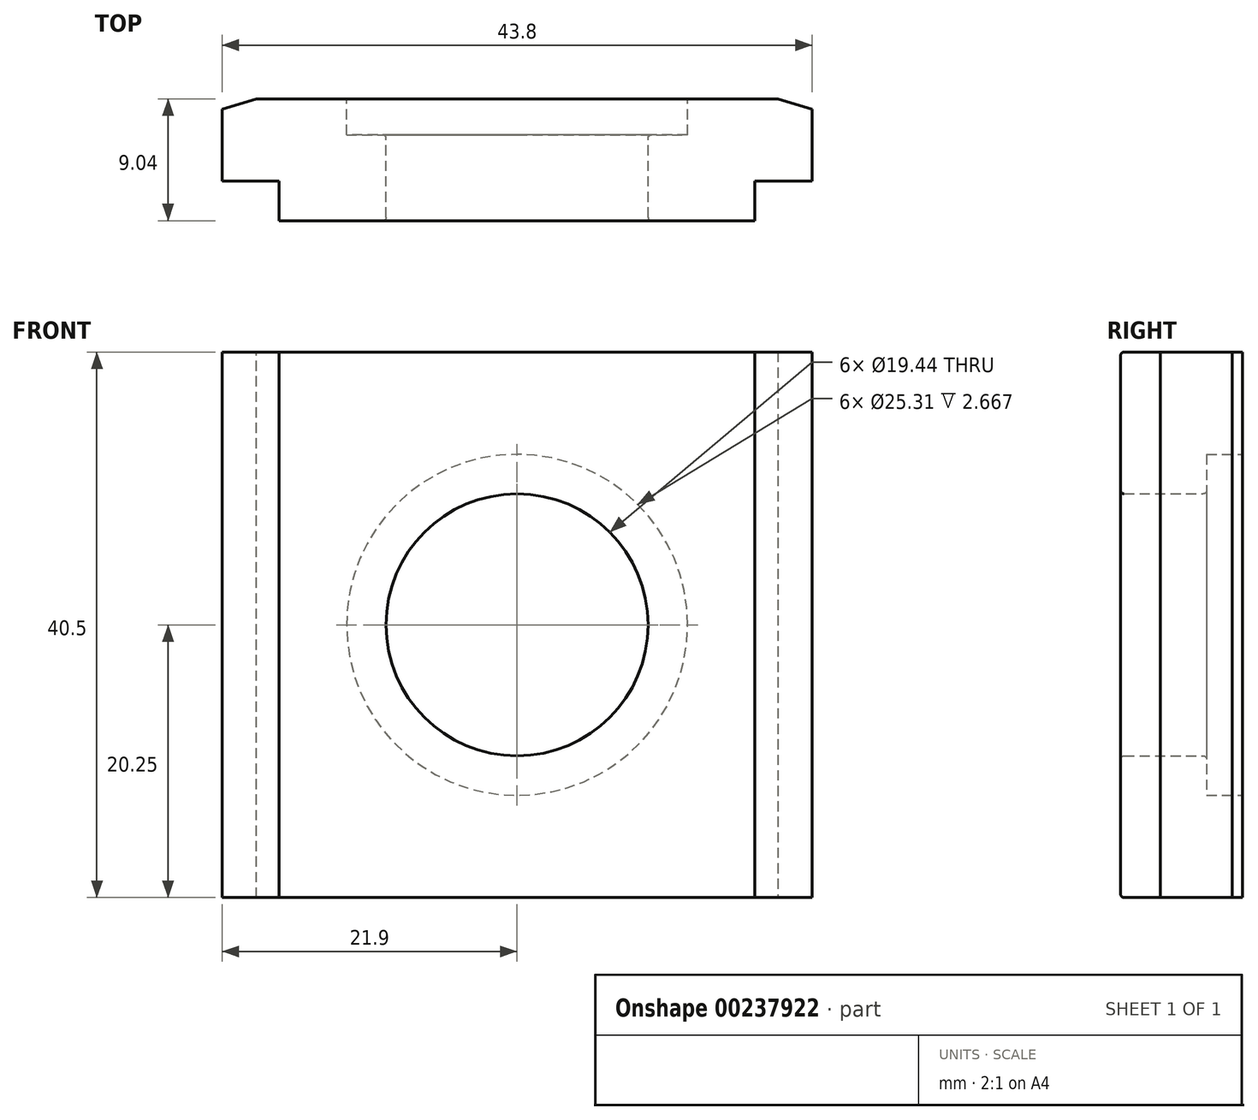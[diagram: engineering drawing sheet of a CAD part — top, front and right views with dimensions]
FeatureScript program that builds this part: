
annotation { "Feature Type Name" : "Feature", "Feature Type Description" : "" }
export const myFeature = defineFeature(function(context is Context, id is Id, definition is map)
    precondition{}
    {
        {
            var Q0;
            Q0=qCreatedBy(makeId("Front.planeOp"),FACE);
            var sketch = newSketch(context, id + "F0", { "sketchPlane" : qUnion([Q0])});
            skLineSegment(sketch, "E0.bottom", {"start": v(21.9, 20.25) * mm, "end": v(-21.9, 20.25) * mm});
            skLineSegment(sketch, "E0.top", {"start": v(21.9, -20.25) * mm, "end": v(-21.9, -20.25) * mm});
            skLineSegment(sketch, "E0.left", {"start": v(21.9, 20.25) * mm, "end": v(21.9, -20.25) * mm});
            skLineSegment(sketch, "E0.right", {"start": v(-21.9, 20.25) * mm, "end": v(-21.9, -20.25) * mm});
            skPoint(sketch, "E0.middle", {"position": v(0, 0) * mm});
            skCircle(sketch, "E1", {"center": v(0, 0) * mm, "radius": 9.72 * mm});
            skSolve(sketch);
        }
        {
            var Q0;
            Q0 = qSketchRegion(id + "F0", true);
            extrude(context, id + "F1", {"entities" : qUnion([Q0]), "depth" : 9.04 * mm});
        }
        {
            var Q0;
            Q0=qCreatedBy(makeId("Top.planeOp"),FACE);
            var sketch = newSketch(context, id + "F2", { "sketchPlane" : qUnion([Q0])});
            skLineSegment(sketch, "E2", {"start": v(0, 0) * mm, "end": v(0, -9.14) * mm});
            skLineSegment(sketch, "E3", {"start": v(0, -9.14) * mm, "end": v(17.65, -9.14) * mm});
            skLineSegment(sketch, "E4", {"start": v(17.65, -9.14) * mm, "end": v(17.65, -6.1) * mm});
            skLineSegment(sketch, "E5", {"start": v(17.65, -6.1) * mm, "end": v(22.7, -6.1) * mm});
            skLineSegment(sketch, "E6", {"start": v(22.7, -6.1) * mm, "end": v(22.7, -9.88) * mm});
            skLineSegment(sketch, "E7", {"start": v(22.7, -9.88) * mm, "end": v(17.65, -9.88) * mm});
            skLineSegment(sketch, "E8", {"start": v(17.65, -9.88) * mm, "end": v(17.65, -9.14) * mm});
            skLineSegment(sketch, "E9.MirrorCS", {"start": v(-17.65, -9.14) * mm, "end": v(-17.65, -6.1) * mm});
            skLineSegment(sketch, "E10.MirrorCS", {"start": v(-17.65, -6.1) * mm, "end": v(-22.7, -6.1) * mm});
            skLineSegment(sketch, "E11.MirrorCS", {"start": v(-22.7, -6.1) * mm, "end": v(-22.7, -9.88) * mm});
            skLineSegment(sketch, "E12.MirrorCS", {"start": v(-22.7, -9.88) * mm, "end": v(-17.65, -9.88) * mm});
            skLineSegment(sketch, "E13.MirrorCS", {"start": v(-17.65, -9.88) * mm, "end": v(-17.65, -9.14) * mm});
            skSolve(sketch);
        }
        {
            var Q0;
            Q0 = qSketchRegion(id + "F2", true);
            extrude(context, id + "F3", {"entities" : qUnion([Q0]), "operationType" : NewBodyOperationType.REMOVE, "endBound" : BoundingType.SYMMETRIC, "depth" : 50.8 * mm});
        }
        {
            var Q0;
            Q0=makeQuery(id+"F1.opExtrude","CAP_EDGE",EDGE,{"disambiguationData":[OSD([sQuery(id+"F0.wireOp",EDGE,"E0.right")])],"isStart":true});
            var Q1;
            Q1=makeQuery(id+"F1.opExtrude","CAP_EDGE",EDGE,{"disambiguationData":[OSD([sQuery(id+"F0.wireOp",EDGE,"E0.left")])],"isStart":true});
            chamfer(context, id + "F4", {"entities" : qUnion([Q0, Q1]), "chamferType" : ChamferType.TWO_OFFSETS, "width1" : 0.76 * mm, "oppositeDirection" : false, "width2" : 2.54 * mm, "tangentPropagation" : true});
        }
        {
            var Q0;
            Q0=makeQuery(id+"F1.opExtrude","CAP_FACE",FACE,{"disambiguationData":[OSD([sQuery(id+"F0.wireOp",EDGE,"E0.bottom"),sQuery(id+"F0.wireOp",EDGE,"E0.top"),sQuery(id+"F0.wireOp",EDGE,"E0.left"),sQuery(id+"F0.wireOp",EDGE,"E0.right"),sQuery(id+"F0.wireOp",EDGE,"E1")])],"isStart":true});
            var sketch = newSketch(context, id + "F5", { "sketchPlane" : qUnion([Q0])});
            skCircle(sketch, "E14", {"center": v(0, 0) * mm, "radius": 12.66 * mm});
            skSolve(sketch);
        }
        {
            var Q0;
            Q0 = qSketchRegion(id + "F5", true);
            extrude(context, id + "F6", {"entities" : qUnion([Q0]), "operationType" : NewBodyOperationType.REMOVE, "oppositeDirection" : true, "depth" : 2.67 * mm});
        }
        {
            var Q0;
            Q0=makeQuery(id+"F6.boolean.opBoolean","COPY",EDGE,{"derivedFrom":makeQuery(id+"F6.opExtrude","CAP_EDGE",EDGE,{"disambiguationData":[OSD([sQuery(id+"F5.wireOp",EDGE,"E14")])],"isStart":true})});
            var Q1;
            Q1=makeQuery(id+"F6.boolean.opBoolean","INTERSECT",EDGE,{"derivedFrom":[makeQuery(id+"F1.opExtrude","SWEPT_FACE",FACE,{"disambiguationData":[OSD([sQuery(id+"F0.wireOp",EDGE,"E1")])]}),makeQuery(id+"F6.opExtrude","CAP_FACE",FACE,{"disambiguationData":[OSD([sQuery(id+"F5.wireOp",EDGE,"E14")])],"isStart":false})]});
            var Q2;
            Q2=makeQuery(id+"F1.opExtrude","CAP_EDGE",EDGE,{"disambiguationData":[OSD([sQuery(id+"F0.wireOp",EDGE,"E0.top")])],"isStart":false});
            var Q3;
            Q3=makeQuery(id+"F1.opExtrude","CAP_EDGE",EDGE,{"disambiguationData":[OSD([sQuery(id+"F0.wireOp",EDGE,"E0.bottom")])],"isStart":false});
            var Q4;
            Q4=makeQuery(id+"F1.opExtrude","CAP_EDGE",EDGE,{"disambiguationData":[OSD([sQuery(id+"F0.wireOp",EDGE,"E1")])],"isStart":false});
            fillet(context, id + "F7", {"entities" : qUnion([Q0, Q1, Q2, Q3, Q4]), "radius" : 0.25 * mm, "tangentPropagation" : true, "allowEdgeOverflow" : false});
        }
    });
